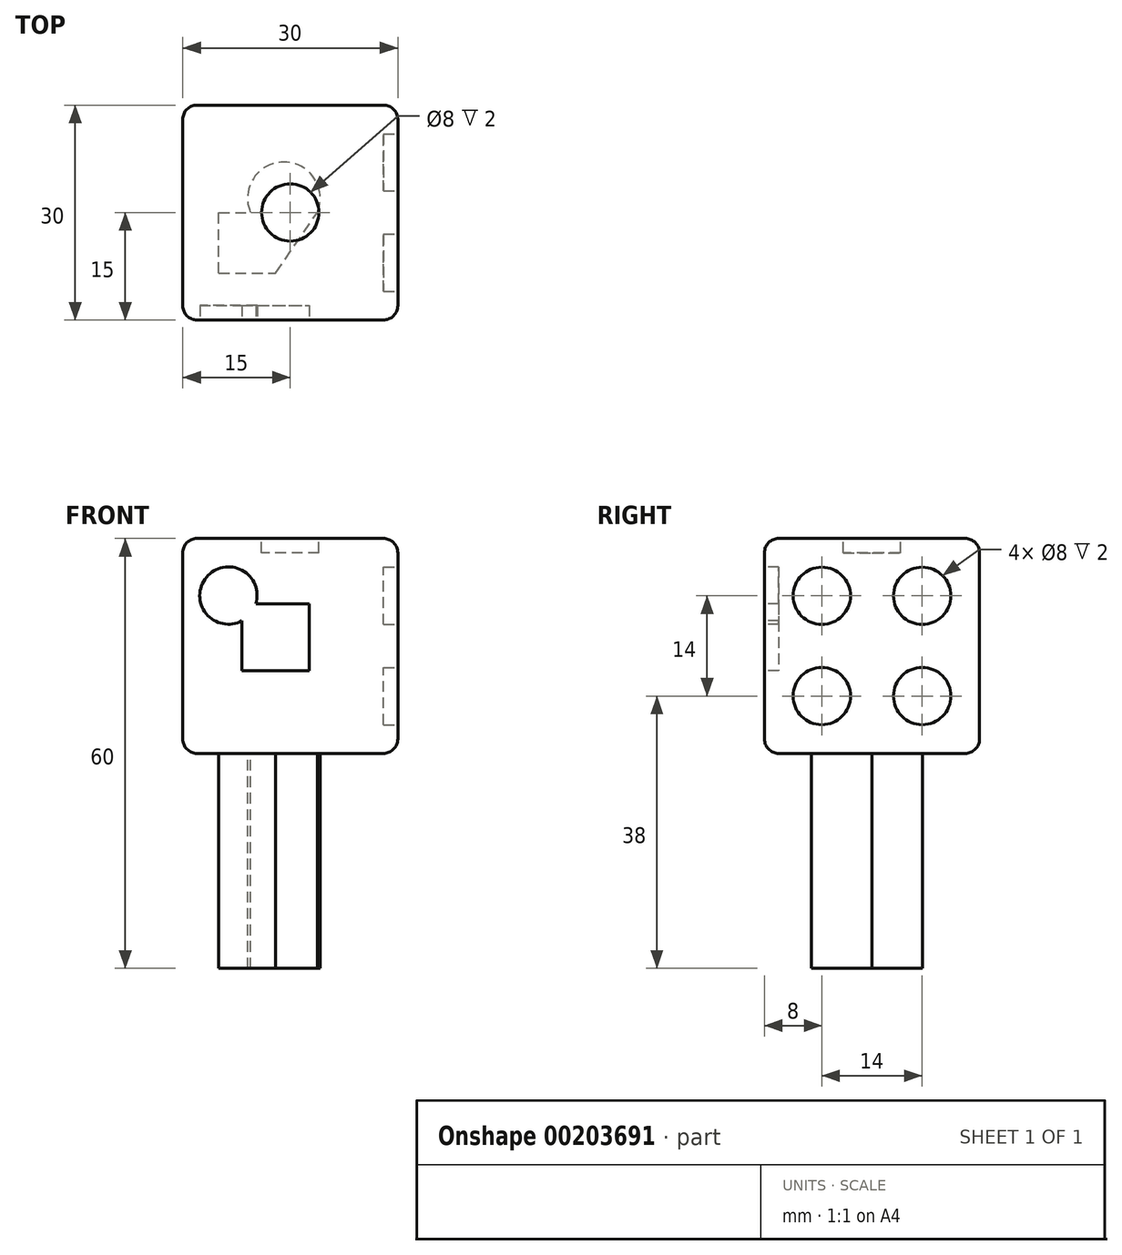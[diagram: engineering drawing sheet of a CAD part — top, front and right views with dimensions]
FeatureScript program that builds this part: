
annotation { "Feature Type Name" : "Feature", "Feature Type Description" : "" }
export const myFeature = defineFeature(function(context is Context, id is Id, definition is map)
    precondition{}
    {
        {
            var Q0;
            Q0=qCreatedBy(makeId("Top.planeOp"),FACE);
            var sketch = newSketch(context, id + "F0", { "sketchPlane" : qUnion([Q0])});
            skLineSegment(sketch, "E0.bottom", {"start": v(-15, -15) * mm, "end": v(15, -15) * mm});
            skLineSegment(sketch, "E0.top", {"start": v(-15, 15) * mm, "end": v(15, 15) * mm});
            skLineSegment(sketch, "E0.left", {"start": v(-15, -15) * mm, "end": v(-15, 15) * mm});
            skLineSegment(sketch, "E0.right", {"start": v(15, -15) * mm, "end": v(15, 15) * mm});
            skPoint(sketch, "E0.middle", {"position": v(0, 0) * mm});
            skSolve(sketch);
        }
        {
            var Q0;
            Q0=makeQuery(id+"F0.imprint","IMPRINT",FACE,{"disambiguationData":[TD([[makeQuery(id+"F0.imprint","IMPRINT",EDGE,{"derivedFrom":sQuery(id+"F0.wireOp",EDGE,"E0.bottom")}),1.0]])]});
            extrude(context, id + "F1", {"entities" : qUnion([Q0]), "endBound" : BoundingType.SYMMETRIC, "depth" : 30 * mm});
        }
        {
            var Q0;
            Q0=makeQuery(id+"F1.opExtrude","CAP_FACE",FACE,{"disambiguationData":[OSD([sQuery(id+"F0.wireOp",EDGE,"E0.bottom"),sQuery(id+"F0.wireOp",EDGE,"E0.top"),sQuery(id+"F0.wireOp",EDGE,"E0.left"),sQuery(id+"F0.wireOp",EDGE,"E0.right")])],"isStart":false});
            var sketch = newSketch(context, id + "F2", { "sketchPlane" : qUnion([Q0])});
            skCircle(sketch, "E1", {"center": v(0, 0) * mm, "radius": 4 * mm});
            skSolve(sketch);
        }
        {
            var Q0;
            Q0=makeQuery(id+"F2.imprint","IMPRINT",FACE,{"disambiguationData":[TD([[makeQuery(id+"F2.imprint","IMPRINT",EDGE,{"derivedFrom":sQuery(id+"F2.wireOp",EDGE,"E1")}),1.0]])]});
            extrude(context, id + "F3", {"entities" : qUnion([Q0]), "operationType" : NewBodyOperationType.REMOVE, "oppositeDirection" : true, "depth" : 2 * mm});
        }
        {
            var Q0;
            Q0=makeQuery(id+"F1.opExtrude","SWEPT_FACE",FACE,{"disambiguationData":[OSD([sQuery(id+"F0.wireOp",EDGE,"E0.right")])]});
            var sketch = newSketch(context, id + "F4", { "sketchPlane" : qUnion([Q0])});
            skCircle(sketch, "E2", {"center": v(-7, 7) * mm, "radius": 4 * mm});
            skCircle(sketch, "E3.0.1.0", {"center": v(-7, -7) * mm, "radius": 4 * mm});
            skCircle(sketch, "E3.1.0.0", {"center": v(7, 7) * mm, "radius": 4 * mm});
            skCircle(sketch, "E3.1.1.0", {"center": v(7, -7) * mm, "radius": 4 * mm});
            skLineSegment(sketch, "E3.direction1", {"start": v(-7, 7) * mm, "end": v(7, 7) * mm, "construction": true});
            skLineSegment(sketch, "E3.direction2", {"start": v(-7, 7) * mm, "end": v(-7, -7) * mm, "construction": true});
            skSolve(sketch);
        }
        {
            var Q0;
            Q0=makeQuery(id+"F4.imprint","IMPRINT",FACE,{"disambiguationData":[TD([[makeQuery(id+"F4.imprint","IMPRINT",EDGE,{"derivedFrom":sQuery(id+"F4.wireOp",EDGE,"E3.0.1.0")}),1.0]])]});
            var Q1;
            Q1=makeQuery(id+"F4.imprint","IMPRINT",FACE,{"disambiguationData":[TD([[makeQuery(id+"F4.imprint","IMPRINT",EDGE,{"derivedFrom":sQuery(id+"F4.wireOp",EDGE,"E3.1.1.0")}),1.0]])]});
            var Q2;
            Q2=makeQuery(id+"F4.imprint","IMPRINT",FACE,{"disambiguationData":[TD([[makeQuery(id+"F4.imprint","IMPRINT",EDGE,{"derivedFrom":sQuery(id+"F4.wireOp",EDGE,"E3.1.0.0")}),1.0]])]});
            var Q3;
            Q3=makeQuery(id+"F4.imprint","IMPRINT",FACE,{"disambiguationData":[TD([[makeQuery(id+"F4.imprint","IMPRINT",EDGE,{"derivedFrom":sQuery(id+"F4.wireOp",EDGE,"E2")}),1.0]])]});
            var Q4;
            Q4=sQuery(id+"F4.wireOp",EDGE,"E3.0.1.0");
            var Q5;
            Q5=sQuery(id+"F4.wireOp",EDGE,"E3.1.1.0");
            var Q6;
            Q6=sQuery(id+"F4.wireOp",EDGE,"E3.1.0.0");
            var Q7;
            Q7=sQuery(id+"F4.wireOp",EDGE,"E2");
            extrude(context, id + "F5", {"entities" : qUnion([Q0, Q1, Q2, Q3]), "operationType" : NewBodyOperationType.REMOVE, "surfaceEntities" : qUnion([Q4, Q5, Q6, Q7]), "oppositeDirection" : true, "depth" : 2 * mm});
        }
        {
            var Q0;
            Q0=makeQuery(id+"F1.opExtrude","SWEPT_FACE",FACE,{"disambiguationData":[OSD([sQuery(id+"F0.wireOp",EDGE,"E0.bottom")])]});
            var sketch = newSketch(context, id + "F6", { "sketchPlane" : qUnion([Q0])});
            skCircle(sketch, "E4", {"center": v(-8.62, 7.03) * mm, "radius": 4 * mm});
            skLineSegment(sketch, "E5.bottom", {"start": v(-6.75, 5.86) * mm, "end": v(2.62, 5.86) * mm});
            skLineSegment(sketch, "E5.top", {"start": v(-6.75, -3.47) * mm, "end": v(2.62, -3.47) * mm});
            skLineSegment(sketch, "E5.left", {"start": v(-6.75, 5.86) * mm, "end": v(-6.75, -3.47) * mm});
            skLineSegment(sketch, "E5.right", {"start": v(2.62, 5.86) * mm, "end": v(2.62, -3.47) * mm});
            skSolve(sketch);
        }
        {
            var Q0;
            Q0 = qSketchRegion(id + "F6", true);
            extrude(context, id + "F7", {"entities" : qUnion([Q0]), "operationType" : NewBodyOperationType.REMOVE, "oppositeDirection" : true, "depth" : 2 * mm});
        }
        {
            var Q0;
            Q0=makeQuery(id+"F1.opExtrude","CAP_EDGE",EDGE,{"disambiguationData":[OSD([sQuery(id+"F0.wireOp",EDGE,"E0.bottom")])],"isStart":false});
            var Q1;
            Q1=makeQuery(id+"F1.opExtrude","SWEPT_EDGE",EDGE,{"disambiguationData":[OSD([sQuery(id+"F0.wireOp",EDGE,"E0.bottom"),sQuery(id+"F0.wireOp",EDGE,"E0.right")])]});
            var Q2;
            Q2=makeQuery(id+"F1.opExtrude","CAP_EDGE",EDGE,{"disambiguationData":[OSD([sQuery(id+"F0.wireOp",EDGE,"E0.right")])],"isStart":false});
            var Q3;
            Q3=makeQuery(id+"F1.opExtrude","CAP_EDGE",EDGE,{"disambiguationData":[OSD([sQuery(id+"F0.wireOp",EDGE,"E0.top")])],"isStart":false});
            var Q4;
            Q4=makeQuery(id+"F1.opExtrude","CAP_EDGE",EDGE,{"disambiguationData":[OSD([sQuery(id+"F0.wireOp",EDGE,"E0.left")])],"isStart":false});
            var Q5;
            Q5=makeQuery(id+"F1.opExtrude","SWEPT_EDGE",EDGE,{"disambiguationData":[OSD([sQuery(id+"F0.wireOp",EDGE,"E0.bottom"),sQuery(id+"F0.wireOp",EDGE,"E0.left")])]});
            var Q6;
            Q6=makeQuery(id+"F1.opExtrude","CAP_EDGE",EDGE,{"disambiguationData":[OSD([sQuery(id+"F0.wireOp",EDGE,"E0.bottom")])],"isStart":true});
            var Q7;
            Q7=makeQuery(id+"F1.opExtrude","CAP_EDGE",EDGE,{"disambiguationData":[OSD([sQuery(id+"F0.wireOp",EDGE,"E0.left")])],"isStart":true});
            var Q8;
            Q8=makeQuery(id+"F1.opExtrude","SWEPT_EDGE",EDGE,{"disambiguationData":[OSD([sQuery(id+"F0.wireOp",EDGE,"E0.top"),sQuery(id+"F0.wireOp",EDGE,"E0.left")])]});
            var Q9;
            Q9=makeQuery(id+"F1.opExtrude","CAP_EDGE",EDGE,{"disambiguationData":[OSD([sQuery(id+"F0.wireOp",EDGE,"E0.top")])],"isStart":true});
            var Q10;
            Q10=makeQuery(id+"F1.opExtrude","CAP_EDGE",EDGE,{"disambiguationData":[OSD([sQuery(id+"F0.wireOp",EDGE,"E0.right")])],"isStart":true});
            var Q11;
            Q11=makeQuery(id+"F1.opExtrude","SWEPT_EDGE",EDGE,{"disambiguationData":[OSD([sQuery(id+"F0.wireOp",EDGE,"E0.top"),sQuery(id+"F0.wireOp",EDGE,"E0.right")])]});
            fillet(context, id + "F8", {"entities" : qUnion([Q0, Q1, Q2, Q3, Q4, Q5, Q6, Q7, Q8, Q9, Q10, Q11]), "radius" : 2 * mm, "tangentPropagation" : true, "allowEdgeOverflow" : false});
        }
        {
            var Q0;
            Q0=makeQuery(id+"F1.opExtrude","CAP_FACE",FACE,{"disambiguationData":[OSD([sQuery(id+"F0.wireOp",EDGE,"E0.bottom"),sQuery(id+"F0.wireOp",EDGE,"E0.top"),sQuery(id+"F0.wireOp",EDGE,"E0.left"),sQuery(id+"F0.wireOp",EDGE,"E0.right")])],"isStart":true});
            var sketch = newSketch(context, id + "F9", { "sketchPlane" : qUnion([Q0])});
            skLineSegment(sketch, "E6.bottom", {"start": v(-9.96, 8.45) * mm, "end": v(-2.04, 8.45) * mm});
            skLineSegment(sketch, "E6.top", {"start": v(-9.96, 0) * mm, "end": v(-5.55, 0) * mm});
            skLineSegment(sketch, "E6.left", {"start": v(-9.96, 8.45) * mm, "end": v(-9.96, 0) * mm});
            skArc(sketch, "E7", {"start": v(-5.55, 0) * mm, "mid": v(2.36, -5.86) * mm, "end": v(-2.04, 2.95) * mm});
            skPoint(sketch, "E8.orphan", {"position": v(-2.04, 0) * mm});
            skFitSpline(sketch, "E9", {"points": [v(-2.04, 8.45) * mm, v(3.76, 0) * mm], "startDerivative": vector(5.8, -8.45) * mm, "endDerivative": vector(5.8, -8.45) * mm});
            skSolve(sketch);
        }
        {
            var Q0;
            {var subQ4=sQuery(id+"F9.wireOp",EDGE,"E6.bottom");Q0=makeQuery(id+"F9.imprint","IMPRINT",FACE,{"disambiguationData":[TD([[makeQuery(id+"F9.imprint","IMPRINT",EDGE,{"derivedFrom":subQ4}),-1.0]])]});}
            extrude(context, id + "F10", {"entities" : qUnion([Q0]), "operationType" : NewBodyOperationType.ADD, "depth" : 30 * mm});
        }
    });
